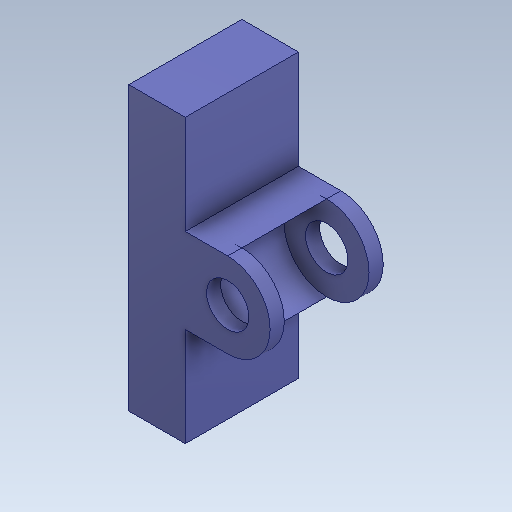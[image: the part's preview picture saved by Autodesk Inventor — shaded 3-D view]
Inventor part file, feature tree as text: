
AUTODESK INVENTOR PART (.ipt)
format: ipt  version: 2021.4 (Build 254397000, 397)  size: 123,904 bytes
history: imported  units: in
note: dims shown in document units (in); Inventor stores cm internally (conversion verified against a paired STEP export)
features: imported_body x1
ambient origin geometry x8: Origin, YZ Plane, XZ Plane, XY Plane, X Axis, Y Axis, Z Axis, Center Point
bodies: Solid1 (imported_parasolid), Body1 (imported_parasolid)
feature tree (1):
  imported_body  NMx_Import_Brep_tag  [imported B-rep: ~16 faces, bbox_mm=[350.0, 1000.0, 400.0]]
